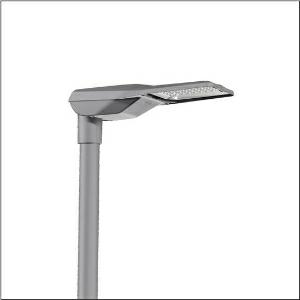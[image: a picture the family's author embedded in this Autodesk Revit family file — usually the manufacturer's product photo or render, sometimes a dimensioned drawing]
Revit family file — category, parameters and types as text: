
# Revit family: streetlight_sl_21_iq_mini___p1_0a_5xe2a31d08gb_969e
name_source: partatom
category: Lighting Fixtures
units: mm (PartAtom-declared; Revit-internal decimal feet)

## family parameters
Cut with Voids When Loaded = No
Host = Face
Light Source = No
Part Type = Normal
Room Calculation Point = No
Round Connector Dimension = Use Diameter
Shared = No

## types (1)
- --- (1 x LED, 5680 lm, 37.1 W, 3000K)
    Apparent Load = 37 VA
    CIE Flux Codes = 21 50 90 100 100
    Color Rendering = 70
    Color Temperature = 3000K
    Default Elevation = 1800 mm
    Description = Streetlight SL 21 iQ mini, mast luminaire, primary light control with lens, of PMMA, primary optical cover: cover, of toughened safety glass, transparent, light distribution: P1.0a, light emission: direct distribution, primary light characteristic: asymmetric, installation type: post-top, side-entry, LED, High Power LED, rated luminous flux: 5.680lm, luminous efficacy: 153lm/W, light colour: 730, colour temperature: 3000K, control gear: iQ-Comfort, control: Auto-Match, Temp-Guard, Lumen-Switch, Night-Set, Smart-Wire, Light-Fading, Desk-Remote (wireless, voltage-free reading and setting of iQ features in the workshop via application-optimized NFC function/RFID function), optimised constant luminous flux control (CLO 2.0), pre-setting: linear dimming characteristic, mains connection: 220..240V, AC, 50/60Hz, start of lifetime: 37W, end of service life: 39W, reduction: 18W, luminaire housing, of diecast aluminium, powder-coated, Siteco® metallic grey (DB 702S), corrosivity category C5 mid according to DIN EN ISO 12944, please order mast flange separately, inclination adjustable: 0°, 5°, 10°, 15°, sealing non-destructively replaceable, multi-level sealing system, length: 628mm, width: 235mm, height: 110mm, mast flange for spigot size: 42mm (side-entry): 5XC10008XM4, 60/48mm (side-entry/post-top): 5XC10108XM2, 76/60mm (side-entry/post-top): 5XC10108XM1, mounting height: 4..8m, protection rating (complete): IP66, insulation class (complete): insulation class II (safety insulation), certification: CE, ENEC, ENEC+, VDE, impact resistance: IK10, permissible operating ambient temperature for outdoor applications: -40..+50°C, standard-compliant lighting for roads and squares, packaging unit: 1 piece

Light Distribution: P1.0a
    Height = 110 mm
    Lamp = 1 x LED
    Lamp Light Flux = 5680 lm
    Lamp Power = 37.1 W
    Lamp count = 1
    Length = 625 mm
    Luminous efficacy = 153 lm/W
    Manufacturer = Siteco
    ModVariant = No
    Model = 5XE2A31D08GB
    Number of Poles = 1
    OnlyDefault = Yes
    Power Factor = 1
    Product Name = Streetlight SL 21 iQ mini | P1.0a
    Product group = mast luminaire | pylon top
    ProductGroupID = 6100
    Protection Class = Protection class II
    Protection Degree = IP 66
    RLX_Detail_Level = 1
    RLX_Emergency_Light_Flux = 0 lm
    RLX_Emergency_Type = 0
    RLX_Emergency_Type_DB = No
    RlxData = <blob elided: 37585 chars, md5=2ec792a9>
    Socket = socket
    Standby Power = 0 W
    System Light Flux = 5680 lm
    System Power = 37 W
    Type Comments = factory setting: luminous flux: 100 % | dim-lin: 254 | 385 mA
    Type Image = l_1003519.jpg
    URL = http://relux.com
    VarID = @adj_208153
    Voltage = 0 V
    Weight = 0.00 kg
    Width = 234 mm

## geometry (parser evidence)
native form markers: Blend x4, Sweep x10
no freeform markers — native parametric forms only
